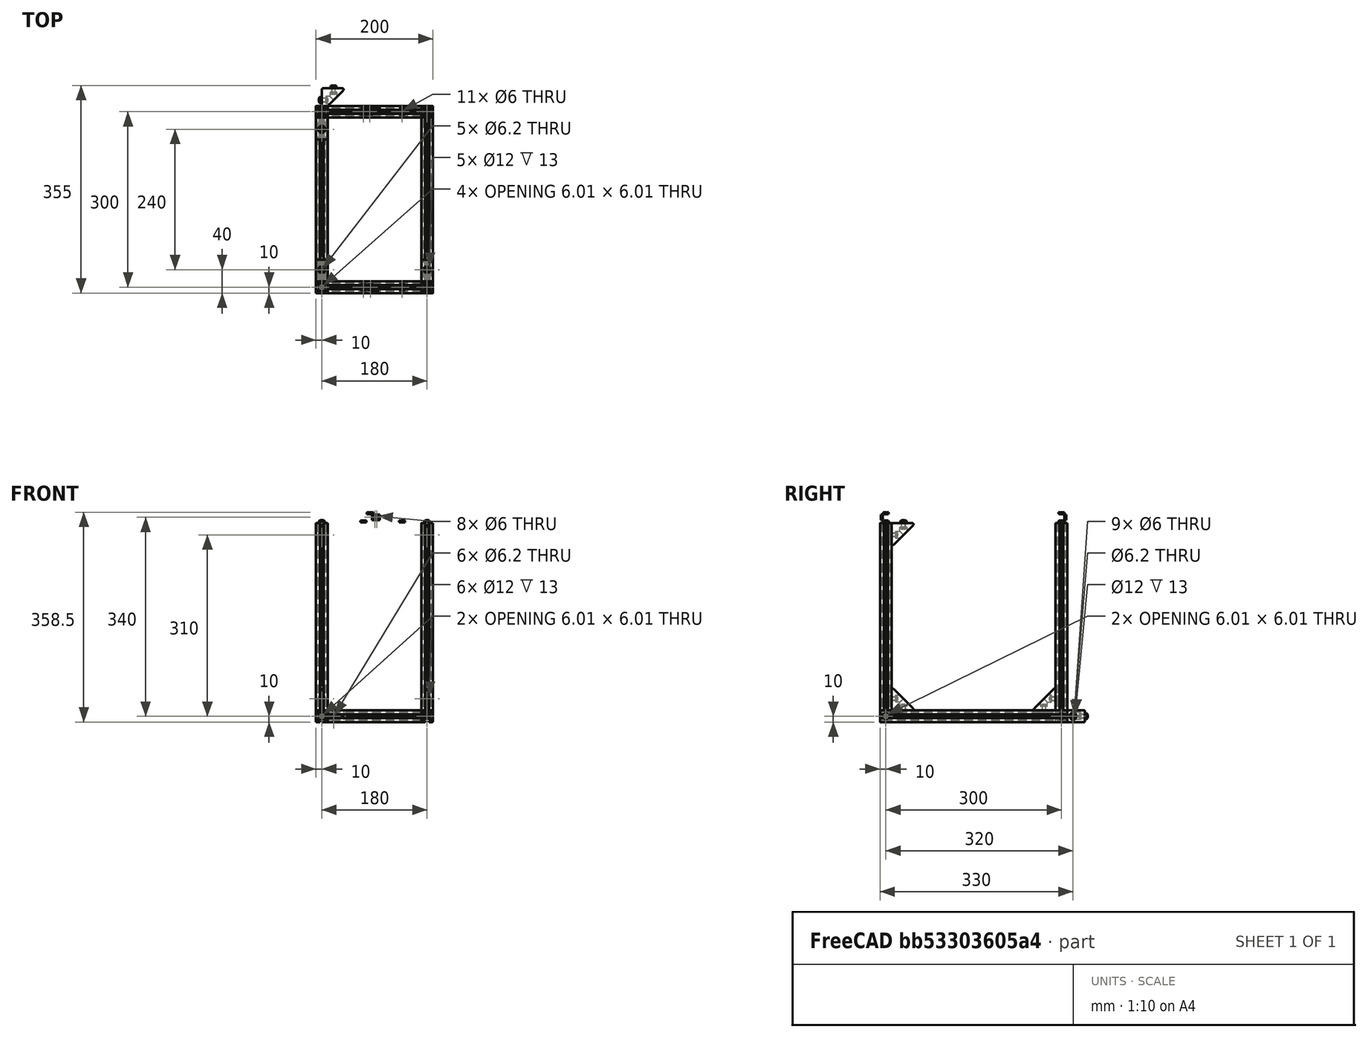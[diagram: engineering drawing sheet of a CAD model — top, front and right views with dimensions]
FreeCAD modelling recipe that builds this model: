
FCSTD DOCUMENT  (FreeCAD 0.17R9796 (Git))
Label: lowerframe1
License: All rights reserved
LicenseURL: http://en.wikipedia.org/wiki/All_rights_reserved
objects: Part::Feature×57, Part::FeaturePython×16, App::Part×6, Part::Compound×5
note: 78 computed .brp shape members not serialized (recipe doc carries the construction recipe); baked Part::Feature solids carry a one-line shape summary decoded from their .brp

FEATURE [Part::Feature] Pocket003001  label="tslot32con"
  Placement = pos=(0,10,10) rot=(1,0,0;1.5708rad)
  shape: bbox 20 x 320 x 20 mm, 150 faces (baked)
FEATURE [Part::Feature] Pocket003002  label="tslot16"
  Placement = pos=(10,0,10) rot=(0,1,0;1.5708rad)
  shape: bbox 160 x 20 x 20 mm, 94 faces (baked)
FEATURE [Part::Feature] Pocket003006  label="tslot16_001"
  Placement = pos=(10,-300,10) rot=(0,1,0;1.5708rad)
  shape: bbox 160 x 20 x 20 mm, 94 faces (baked)
FEATURE [Part::Feature] Pocket003007  label="tslot32con_001"
  Placement = pos=(180,-310,10) rot=(0,0.707107,0.707107;3.14159rad)
  shape: bbox 20 x 320 x 20 mm, 150 faces (baked)
FEATURE [Part::FeaturePython] Screw  label="M6x25-Screw"  # Fasteners workbench fastener (typed FeaturePython)
  Placement = pos=(-4,0,10) rot=(0,-1,0;1.5708rad)
  diameter = 7
  invert = false
  length = 6
  matchOuter = false
  offset = 0
  thread = false
  type = 15
FEATURE [Part::FeaturePython] Screw001  label="M6x25-Screw004"  # Fasteners workbench fastener (typed FeaturePython)
  Placement = pos=(-4,-300,10) rot=(0,-1,0;1.5708rad)
  diameter = 7
  invert = false
  length = 6
  matchOuter = false
  offset = 0
  thread = false
  type = 15
FEATURE [Part::FeaturePython] Screw002  label="M6x25-Screw005"  # Fasteners workbench fastener (typed FeaturePython)
  Placement = pos=(184,0,10) rot=(0,1,0;1.5708rad)
  diameter = 7
  invert = false
  length = 6
  matchOuter = false
  offset = 0
  thread = false
  type = 15
FEATURE [Part::FeaturePython] Screw004  label="M6x25-Screw006"  # Fasteners workbench fastener (typed FeaturePython)
  Placement = pos=(184,-300,10) rot=(0,1,0;1.5708rad)
  diameter = 7
  invert = false
  length = 6
  matchOuter = false
  offset = 0
  thread = false
  type = 15
FEATURE [App::Part] Part  label="lower_frame"
  Group = -> [Pocket003001,Pocket003002,Pocket003006,Pocket003007,Screw,Screw001,Screw002,Screw004]
  License = CC BY 3.0
  LicenseURL = http://creativecommons.org/licenses/by/3.0/
  Origin = -> PartOrigin
FEATURE [Part::Feature] Pocket003008  label="tslot32con001"
  Placement = pos=(0,10,10) rot=(1,0,0;1.5708rad)
  shape: bbox 20 x 320 x 20 mm, 150 faces (baked)
FEATURE [Part::Feature] Pocket003009  label="tslot041"
  Placement = pos=(10,0,10) rot=(0,1,0;1.5708rad)
  shape: bbox 160 x 20 x 20 mm, 94 faces (baked)
FEATURE [Part::Feature] Pocket003010  label="tslot16_002"
  Placement = pos=(10,-300,10) rot=(0,1,0;1.5708rad)
  shape: bbox 160 x 20 x 20 mm, 94 faces (baked)
FEATURE [Part::Feature] Pocket003011  label="tslot32con_002"
  Placement = pos=(180,-310,10) rot=(0,0.707107,0.707107;3.14159rad)
  shape: bbox 20 x 320 x 20 mm, 150 faces (baked)
FEATURE [Part::FeaturePython] Screw005  label="M6x25-Screw007"  # Fasteners workbench fastener (typed FeaturePython)
  Placement = pos=(-4,0,10) rot=(0,-1,0;1.5708rad)
  diameter = 7
  invert = false
  length = 6
  matchOuter = false
  offset = 0
  thread = false
  type = 15
FEATURE [Part::FeaturePython] Screw006  label="M6x25-Screw008"  # Fasteners workbench fastener (typed FeaturePython)
  Placement = pos=(-4,-300,10) rot=(0,-1,0;1.5708rad)
  diameter = 7
  invert = false
  length = 6
  matchOuter = false
  offset = 0
  thread = false
  type = 15
FEATURE [Part::FeaturePython] Screw007  label="M6x25-Screw011"  # Fasteners workbench fastener (typed FeaturePython)
  Placement = pos=(184,0,10) rot=(0,1,0;1.5708rad)
  diameter = 7
  invert = false
  length = 6
  matchOuter = false
  offset = 0
  thread = false
  type = 15
FEATURE [Part::FeaturePython] Screw008  label="M6x25-Screw010"  # Fasteners workbench fastener (typed FeaturePython)
  Placement = pos=(184,-300,10) rot=(0,1,0;1.5708rad)
  diameter = 7
  invert = false
  length = 6
  matchOuter = false
  offset = 0
  thread = false
  type = 15
FEATURE [App::Part] Part001  label="upper_frame"
  Group = -> [Pocket003008,Pocket003009,Pocket003010,Pocket003011,Screw005,Screw006,Screw007,Screw008]
  License = CC BY 3.0
  LicenseURL = http://creativecommons.org/licenses/by/3.0/
  Origin = -> PartOrigin001
  Placement = pos=(0,0,340) rot=(0,0,1;0rad)
FEATURE [Part::Feature] Fillet004001  label="Fillet005"
  shape: bbox 37.5 x 37.5 x 20 mm, 26 faces (baked)
FEATURE [Part::FeaturePython] Screw009  label="M6x12-Screw"  # Fasteners workbench fastener (typed FeaturePython)
  Placement = pos=(7,20,10) rot=(0,1,0;1.5708rad)
  diameter = 4
  invert = false
  length = 1
  matchOuter = false
  offset = 0
  thread = false
  type = 20
FEATURE [Part::Feature] Body001  label="m6nutplate"
  Placement = pos=(-1.5,15,5) rot=(0,-1,0;1.5708rad)
  shape: bbox 3 x 10 x 10 mm, 9 faces (baked)
FEATURE [App::Part] Part002  label="cornerstonescrewnut"
  License = CC BY 3.0
  LicenseURL = http://creativecommons.org/licenses/by/3.0/
  Origin = -> PartOrigin002
  Placement = pos=(10,-50,20) rot=(0,-1,0;1.5708rad)
FEATURE [Part::FeaturePython] Screw010  label="M6x12-Screw001"  # Fasteners workbench fastener (typed FeaturePython)
  Placement = pos=(20,33,10) rot=(1,0,0;1.5708rad)
  diameter = 4
  invert = false
  length = 1
  matchOuter = false
  offset = 0
  thread = false
  type = 20
FEATURE [Part::Feature] Body002  label="m6nutplate001"
  Placement = pos=(15,41.5,5) rot=(0.57735,0.57735,0.57735;4.18879rad)
  shape: bbox 10 x 3 x 10 mm, 9 faces (baked)
FEATURE [Part::Feature] Fillet004002  label="Fillet006"
  shape: bbox 37.5 x 37.5 x 20 mm, 26 faces (baked)
FEATURE [Part::FeaturePython] Screw011  label="M6x12-Screw002"  # Fasteners workbench fastener (typed FeaturePython)
  Placement = pos=(7,20,10) rot=(0,1,0;1.5708rad)
  diameter = 4
  invert = false
  length = 1
  matchOuter = false
  offset = 0
  thread = false
  type = 20
FEATURE [Part::Feature] Body003  label="m6nutplate002"
  Placement = pos=(-1.5,15,5) rot=(0,-1,0;1.5708rad)
  shape: bbox 3 x 10 x 10 mm, 9 faces (baked)
FEATURE [Part::FeaturePython] Screw012  label="M6x12-Screw003"  # Fasteners workbench fastener (typed FeaturePython)
  Placement = pos=(20,33,10) rot=(1,0,0;1.5708rad)
  diameter = 4
  invert = false
  length = 1
  matchOuter = false
  offset = 0
  thread = false
  type = 20
FEATURE [Part::Feature] Body004  label="m6nutplate003"
  Placement = pos=(15,41.5,5) rot=(0.57735,0.57735,0.57735;4.18879rad)
  shape: bbox 10 x 3 x 10 mm, 9 faces (baked)
FEATURE [App::Part] Part003  label="cornerstonescrewnut001"
  Group = -> [Body003,Screw011,Fillet004002,Screw012,Body004,PartOrigin002,Body001,Screw009,Fillet004001,Screw010,Body002,Part002]
  License = CC BY 3.0
  LicenseURL = http://creativecommons.org/licenses/by/3.0/
  Origin = -> PartOrigin003
  Placement = pos=(190,-50,20) rot=(0,-1,0;1.5708rad)
FEATURE [Part::Feature] Fillet004003  label="Fillet007"
  shape: bbox 37.5 x 37.5 x 20 mm, 26 faces (baked)
FEATURE [Part::FeaturePython] Screw013  label="M6x12-Screw004"  # Fasteners workbench fastener (typed FeaturePython)
  Placement = pos=(7,20,10) rot=(0,1,0;1.5708rad)
  diameter = 4
  invert = false
  length = 1
  matchOuter = false
  offset = 0
  thread = false
  type = 20
FEATURE [Part::Feature] Body005  label="m6nutplate004"
  Placement = pos=(-1.5,15,5) rot=(0,-1,0;1.5708rad)
  shape: bbox 3 x 10 x 10 mm, 9 faces (baked)
FEATURE [Part::FeaturePython] Screw014  label="M6x12-Screw005"  # Fasteners workbench fastener (typed FeaturePython)
  Placement = pos=(20,33,10) rot=(1,0,0;1.5708rad)
  diameter = 4
  invert = false
  length = 1
  matchOuter = false
  offset = 0
  thread = false
  type = 20
FEATURE [Part::Feature] Body006  label="m6nutplate005"
  Placement = pos=(15,41.5,5) rot=(0.57735,0.57735,0.57735;4.18879rad)
  shape: bbox 10 x 3 x 10 mm, 9 faces (baked)
FEATURE [App::Part] Part004  label="cornerstonescrewnut002"
  Group = -> [Body005,Screw013,Fillet004003,Screw014,Body006]
  License = CC BY 3.0
  LicenseURL = http://creativecommons.org/licenses/by/3.0/
  Origin = -> PartOrigin004
  Placement = pos=(-10,-50,340) rot=(0,1,0;1.5708rad)
FEATURE [Part::Feature] Fillet004004  label="Fillet008"
  shape: bbox 37.5 x 37.5 x 20 mm, 26 faces (baked)
FEATURE [Part::FeaturePython] Screw015  label="M6x12-Screw006"  # Fasteners workbench fastener (typed FeaturePython)
  Placement = pos=(7,20,10) rot=(0,1,0;1.5708rad)
  diameter = 4
  invert = false
  length = 1
  matchOuter = false
  offset = 0
  thread = false
  type = 20
FEATURE [Part::Feature] Body007  label="m6nutplate006"
  Placement = pos=(-1.5,15,5) rot=(0,-1,0;1.5708rad)
  shape: bbox 3 x 10 x 10 mm, 9 faces (baked)
FEATURE [Part::FeaturePython] Screw016  label="M6x12-Screw007"  # Fasteners workbench fastener (typed FeaturePython)
  Placement = pos=(20,33,10) rot=(1,0,0;1.5708rad)
  diameter = 4
  invert = false
  length = 1
  matchOuter = false
  offset = 0
  thread = false
  type = 20
FEATURE [Part::Feature] Body008  label="m6nutplate007"
  Placement = pos=(15,41.5,5) rot=(0.57735,0.57735,0.57735;4.18879rad)
  shape: bbox 10 x 3 x 10 mm, 9 faces (baked)
FEATURE [App::Part] Part005  label="cornerstonescrewnut003"
  Group = -> [Body007,Screw015,Fillet004004,Screw016,Body008]
  License = CC BY 3.0
  LicenseURL = http://creativecommons.org/licenses/by/3.0/
  Origin = -> PartOrigin005
  Placement = pos=(170,-50,340) rot=(0,1,0;1.5708rad)
FEATURE [Part::Feature] Body009001  label="m6nutplate010"
  Placement = pos=(-1.5,15,5) rot=(0,-1,0;1.5708rad)
  shape: bbox 3 x 10 x 10 mm, 9 faces (baked)
FEATURE [Part::Feature] Body010001  label="m6nutplate011"
  Placement = pos=(15,41.5,5) rot=(0.57735,0.57735,0.57735;4.18879rad)
  shape: bbox 10 x 3 x 10 mm, 9 faces (baked)
FEATURE [Part::Feature] Screw018001  label="M6x12-Screw010"
  Placement = pos=(20,33,10) rot=(1,0,0;1.5708rad)
  shape: bbox 10.5 x 15.3 x 10.5 mm, 15 faces (baked)
FEATURE [Part::Feature] Screw017001  label="M6x12-Screw011"
  Placement = pos=(7,20,10) rot=(0,1,0;1.5708rad)
  shape: bbox 15.3 x 10.5 x 10.5 mm, 15 faces (baked)
FEATURE [Part::Feature] Fillet004005001  label="Fillet010"
  shape: bbox 37.5 x 37.5 x 20 mm, 26 faces (baked)
FEATURE [Part::Compound] Compound
  Links = -> [Body009001,Fillet004005001,Screw017001,Body010001,Screw018001]
  Placement = pos=(10,-250,340) rot=(0.707107,0,-0.707107;3.14159rad)
FEATURE [Part::Feature] Body010002  label="m6nutplate012"
  Placement = pos=(-1.5,15,5) rot=(0,-1,0;1.5708rad)
  shape: bbox 3 x 10 x 10 mm, 9 faces (baked)
FEATURE [Part::Feature] Body010003  label="m6nutplate013"
  Placement = pos=(15,41.5,5) rot=(0.57735,0.57735,0.57735;4.18879rad)
  shape: bbox 10 x 3 x 10 mm, 9 faces (baked)
FEATURE [Part::Feature] Screw018002  label="M6x12-Screw012"
  Placement = pos=(20,33,10) rot=(1,0,0;1.5708rad)
  shape: bbox 10.5 x 15.3 x 10.5 mm, 15 faces (baked)
FEATURE [Part::Feature] Screw018003  label="M6x12-Screw013"
  Placement = pos=(7,20,10) rot=(0,1,0;1.5708rad)
  shape: bbox 15.3 x 10.5 x 10.5 mm, 15 faces (baked)
FEATURE [Part::Feature] Fillet004005002  label="Fillet011"
  shape: bbox 37.5 x 37.5 x 20 mm, 26 faces (baked)
FEATURE [Part::Compound] Compound001
  Links = -> [Body010002,Fillet004005002,Screw018003,Body010003,Screw018002]
  Placement = pos=(190,-250,340) rot=(0.707107,0,-0.707107;3.14159rad)
FEATURE [Part::Feature] Body010004  label="m6nutplate014"
  Placement = pos=(-1.5,15,5) rot=(0,-1,0;1.5708rad)
  shape: bbox 3 x 10 x 10 mm, 9 faces (baked)
FEATURE [Part::Feature] Body010005  label="m6nutplate015"
  Placement = pos=(15,41.5,5) rot=(0.57735,0.57735,0.57735;4.18879rad)
  shape: bbox 10 x 3 x 10 mm, 9 faces (baked)
FEATURE [Part::Feature] Screw018004  label="M6x12-Screw014"
  Placement = pos=(20,33,10) rot=(1,0,0;1.5708rad)
  shape: bbox 10.5 x 15.3 x 10.5 mm, 15 faces (baked)
FEATURE [Part::Feature] Screw018005  label="M6x12-Screw015"
  Placement = pos=(7,20,10) rot=(0,1,0;1.5708rad)
  shape: bbox 15.3 x 10.5 x 10.5 mm, 15 faces (baked)
FEATURE [Part::Feature] Fillet004005003  label="Fillet012"
  shape: bbox 37.5 x 37.5 x 20 mm, 26 faces (baked)
FEATURE [Part::Compound] Compound002
  Links = -> [Body010004,Fillet004005003,Screw018005,Body010005,Screw018004]
  Placement = pos=(10,-290,60) rot=(0.57735,0.57735,-0.57735;4.18879rad)
FEATURE [Part::Feature] Body010006  label="m6nutplate016"
  Placement = pos=(-1.5,15,5) rot=(0,-1,0;1.5708rad)
  shape: bbox 3 x 10 x 10 mm, 9 faces (baked)
FEATURE [Part::Feature] Body010007  label="m6nutplate017"
  Placement = pos=(15,41.5,5) rot=(0.57735,0.57735,0.57735;4.18879rad)
  shape: bbox 10 x 3 x 10 mm, 9 faces (baked)
FEATURE [Part::Feature] Screw018006  label="M6x12-Screw016"
  Placement = pos=(20,33,10) rot=(1,0,0;1.5708rad)
  shape: bbox 10.5 x 15.3 x 10.5 mm, 15 faces (baked)
FEATURE [Part::Feature] Screw018007  label="M6x12-Screw017"
  Placement = pos=(7,20,10) rot=(0,1,0;1.5708rad)
  shape: bbox 15.3 x 10.5 x 10.5 mm, 15 faces (baked)
FEATURE [Part::Feature] Fillet004005004  label="Fillet013"
  shape: bbox 37.5 x 37.5 x 20 mm, 26 faces (baked)
FEATURE [Part::Compound] Compound003
  Links = -> [Body010006,Fillet004005004,Screw018007,Body010007,Screw018006]
  Placement = pos=(190,-290,60) rot=(0.57735,0.57735,-0.57735;4.18879rad)
FEATURE [Part::Feature] Pocket001001  label="tslot32"
  Placement = pos=(0,0,20) rot=(0,0,1;0rad)
  shape: bbox 20 x 20 x 320 mm, 94 faces (baked)
FEATURE [Part::Feature] Body010008  label="m6nutplate018"
  Placement = pos=(-1.5,15,5) rot=(0,-1,0;1.5708rad)
  shape: bbox 3 x 10 x 10 mm, 9 faces (baked)
FEATURE [Part::Feature] Body010009  label="m6nutplate019"
  Placement = pos=(15,41.5,5) rot=(0.57735,0.57735,0.57735;4.18879rad)
  shape: bbox 10 x 3 x 10 mm, 9 faces (baked)
FEATURE [Part::Feature] Screw018008  label="M6x12-Screw018"
  Placement = pos=(20,33,10) rot=(1,0,0;1.5708rad)
  shape: bbox 10.5 x 15.3 x 10.5 mm, 15 faces (baked)
FEATURE [Part::Feature] Screw018009  label="M6x12-Screw019"
  Placement = pos=(7,20,10) rot=(0,1,0;1.5708rad)
  shape: bbox 15.3 x 10.5 x 10.5 mm, 15 faces (baked)
FEATURE [Part::Feature] Fillet004005005  label="Fillet014"
  shape: bbox 37.5 x 37.5 x 20 mm, 26 faces (baked)
FEATURE [Part::Compound] Compound004
  Links = -> [Body010008,Fillet004005005,Screw018009,Body010009,Screw018008]
  Placement = pos=(-10,-10,60) rot=(0.57735,-0.57735,0.57735;4.18879rad)
FEATURE [Part::Feature] Pocket003012  label="tslot32_001"
  Placement = pos=(0,-300,20) rot=(0,0,1;0rad)
  shape: bbox 20 x 20 x 320 mm, 94 faces (baked)
FEATURE [Part::Feature] Pocket003013  label="tslot32_002"
  Placement = pos=(180,0,20) rot=(0,0,1;0rad)
  shape: bbox 20 x 20 x 320 mm, 94 faces (baked)
FEATURE [Part::Feature] Pocket003014  label="tslot32_003"
  Placement = pos=(180,-300,20) rot=(0,0,1;0rad)
  shape: bbox 20 x 20 x 320 mm, 94 faces (baked)
FEATURE [Part::Feature] Chamfer001001  label="m6nutplate020"
  Placement = pos=(88,-295,358.5) rot=(-0.707107,0.707107,0;3.14159rad)
  shape: bbox 10 x 10 x 3 mm, 9 faces (baked)
FEATURE [Part::Feature] Chamfer001002  label="m6nutplate021"
  Placement = pos=(96,-308.5,355) rot=(0.57735,-0.57735,-0.57735;4.18879rad)
  shape: bbox 10 x 3 x 10 mm, 9 faces (baked)
FEATURE [Part::Feature] Chamfer001003  label="m6nutplate022"
  Placement = pos=(87,5,358.5) rot=(0.707107,-0.707107,0;3.14159rad)
  shape: bbox 10 x 10 x 3 mm, 9 faces (baked)
FEATURE [Part::Feature] Chamfer001004  label="m6nutplate023"
  Placement = pos=(99,8.4,345) rot=(0.57735,-0.57735,0.57735;2.0944rad)
  shape: bbox 10 x 3 x 10 mm, 9 faces (baked)
FEATURE [Part::Feature] Chamfer001005  label="m6nutplate024"
  Placement = pos=(76,-305,341.6) rot=(0,0,1;1.5708rad)
  shape: bbox 10 x 10 x 3 mm, 9 faces (baked)
FEATURE [Part::Feature] Chamfer001006  label="m6nutplate025"
  Placement = pos=(142,-305,341.6) rot=(0,0,1;1.5708rad)
  shape: bbox 10 x 10 x 3 mm, 9 faces (baked)
FEATURE [Part::Feature] Chamfer001007  label="m6nutplate026"
  Placement = pos=(142,-5,341.6) rot=(0,0,1;1.5708rad)
  shape: bbox 10 x 10 x 3 mm, 9 faces (baked)
FEATURE [Part::Feature] Chamfer001008  label="m6nutplate027"
  Placement = pos=(76,-5,341.6) rot=(0,0,1;1.5708rad)
  shape: bbox 10 x 10 x 3 mm, 9 faces (baked)
